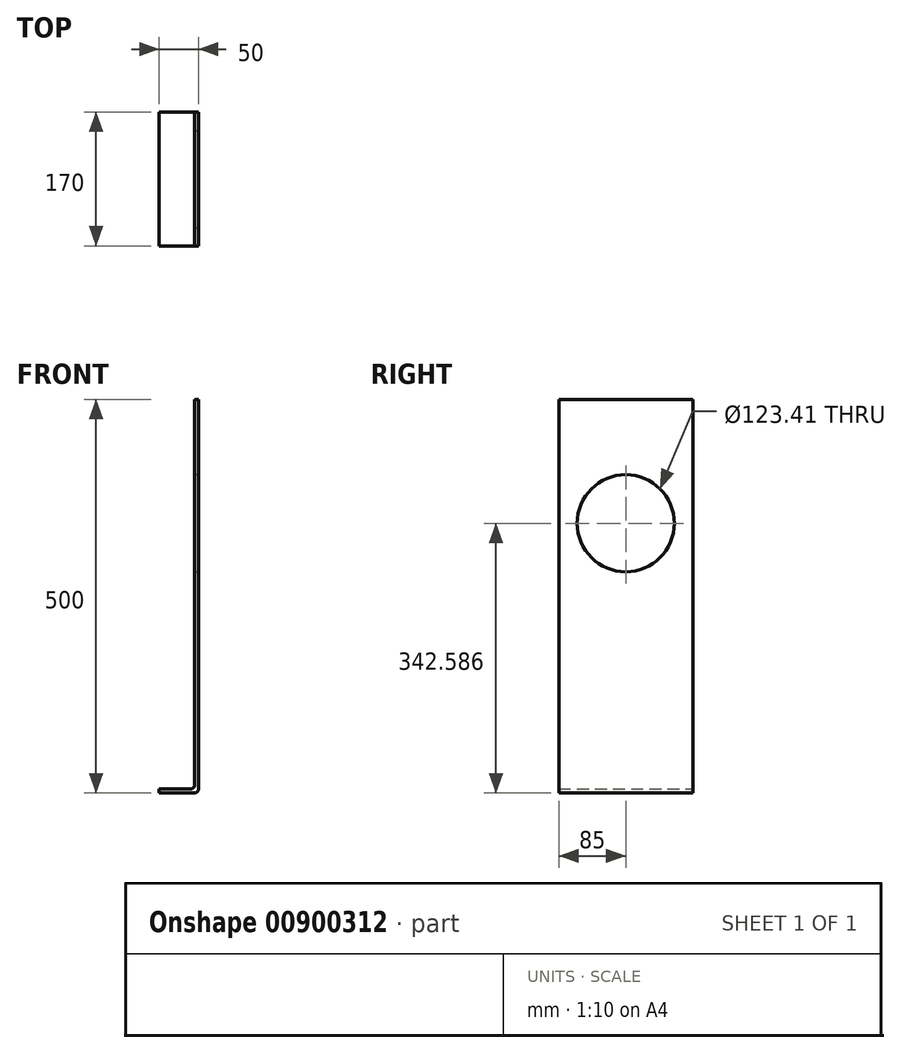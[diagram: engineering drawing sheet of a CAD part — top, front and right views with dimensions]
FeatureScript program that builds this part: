
annotation { "Feature Type Name" : "Feature", "Feature Type Description" : "" }
export const myFeature = defineFeature(function(context is Context, id is Id, definition is map)
    precondition{}
    {
        {
            var Q0;
            Q0=qCreatedBy(makeId("Front.planeOp"),FACE);
            var sketch = newSketch(context, id + "F0", { "sketchPlane" : qUnion([Q0])});
            skLineSegment(sketch, "E0", {"start": v(-41.54, 506.28) * mm, "end": v(-41.54, 11.28) * mm});
            skLineSegment(sketch, "E1", {"start": v(-46.54, 6.28) * mm, "end": v(-91.54, 6.28) * mm});
            skLineSegment(sketch, "E2.0", {"start": v(-46.54, 506.28) * mm, "end": v(-46.54, 16.28) * mm});
            skLineSegment(sketch, "E3.0", {"start": v(-51.54, 11.28) * mm, "end": v(-91.54, 11.28) * mm});
            skArc(sketch, "E4.filletArc", {"start": v(-51.54, 11.28) * mm, "mid": v(-48, 12.75) * mm, "end": v(-46.54, 16.28) * mm});
            skLineSegment(sketch, "E5", {"start": v(-91.54, 11.28) * mm, "end": v(-91.54, 6.28) * mm});
            skLineSegment(sketch, "E6", {"start": v(-46.54, 506.28) * mm, "end": v(-41.54, 506.28) * mm});
            skPoint(sketch, "E7.visualSharp", {"position": v(-41.54, 6.28) * mm});
            skArc(sketch, "E7.filletArc", {"start": v(-46.54, 6.28) * mm, "mid": v(-43, 7.75) * mm, "end": v(-41.54, 11.28) * mm});
            skSolve(sketch);
        }
        {
            var Q0;
            Q0=makeQuery(id+"F0.imprint","IMPRINT",FACE,{"disambiguationData":[TD([[makeQuery(id+"F0.imprint","IMPRINT",EDGE,{"derivedFrom":sQuery(id+"F0.wireOp",EDGE,"E0")}),-1.0]])]});
            extrude(context, id + "F1", {"entities" : qUnion([Q0]), "depth" : 170 * mm, "offsetDistance" : 25 * mm});
        }
        {
            var Q0;
            Q0=makeQuery(id+"F1.opExtrude","SWEPT_FACE",FACE,{"disambiguationData":[OSD([sQuery(id+"F0.wireOp",EDGE,"E0")])]});
            var sketch = newSketch(context, id + "F2", { "sketchPlane" : qUnion([Q0])});
            skLineSegment(sketch, "E8", {"start": v(-85, 11.28) * mm, "end": v(-85, -26.68) * mm});
            skLineSegment(sketch, "E9", {"start": v(-85, 11.28) * mm, "end": v(-85, 0) * mm});
            skLineSegment(sketch, "E10", {"start": v(-85, 6.34) * mm, "end": v(-85, 348.87) * mm});
            skCircle(sketch, "E11", {"center": v(-85, 348.87) * mm, "radius": 61.7 * mm});
            skSolve(sketch);
        }
        {
            var Q0;
            Q0=makeQuery(id+"F2.imprint","IMPRINT",FACE,{"disambiguationData":[TD([[makeQuery(id+"F2.imprint","IMPRINT",EDGE,{"derivedFrom":sQuery(id+"F2.wireOp",EDGE,"E11")}),1.0]])]});
            extrude(context, id + "F3", {"entities" : qUnion([Q0]), "operationType" : NewBodyOperationType.REMOVE, "oppositeDirection" : true, "depth" : 5 * mm, "offsetDistance" : 25 * mm});
        }
    });
